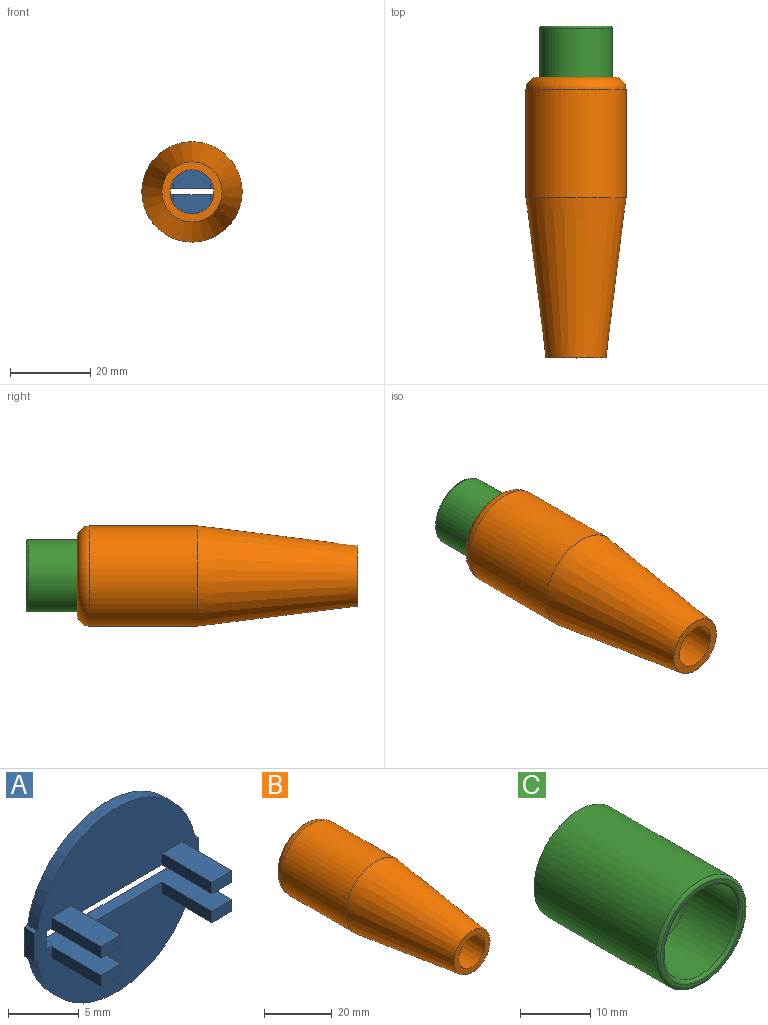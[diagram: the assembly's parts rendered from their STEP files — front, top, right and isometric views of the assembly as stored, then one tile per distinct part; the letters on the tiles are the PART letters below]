
ASSEMBLY  parts=3 mates=2
PART A: 30 faces, bbox 16.5x6x16 mm
  f0: plane 2.5x1mm, normal (1,0,0), area 2.5mm2, adj f1,f11,f12,f13
  f1: plane 1x0.35mm, normal (0,0,1), area 0.3mm2, adj f0,f2,f12,f13
  f2: cylinder r=8mm len=15.8mm, axis (0,1,0), area 22.6mm2, adj f1,f3,f12,f13
  f3: plane 1x0.35mm, normal (0,0,1), area 0.3mm2, adj f2,f4,f12,f13
  f4: plane 2.5x1mm, normal (-1,0,0), area 2.5mm2, adj f3,f5,f12,f13
  f5: plane 1x0.35mm, normal (0,0,-1), area 0.3mm2, adj f4,f6,f12,f13
  f6: cylinder r=8mm len=15.8mm, axis (0,1,0), area 22.6mm2, adj f5,f11,f12,f13
  f7: plane 1.5x1mm, normal (-1,0,0), area 1.5mm2, adj f8,f10,f12,f13
  f8: plane 14x6mm, normal (0,0,1), area 34mm2, adj f7,f9,f12,f13,f18,f19,f21,f22
  f9: plane 1.5x1mm, normal (1,0,0), area 1.5mm2, adj f8,f10,f12,f13
  f10: plane 14x6mm, normal (0,0,-1), area 34mm2, adj f7,f9,f12,f13,f14,f16,f17,f26
  f11: plane 1x0.35mm, normal (0,0,-1), area 0.3mm2, adj f0,f6,f12,f13
  f12: plane 16.5x16mm, normal (0,-1,0), area 173.5mm2, adj f0,f1,f2,f3,f4,f5,f6,f7
  f13: plane 16.5x16mm, normal (0,1,0), area 181.5mm2, adj f0,f1,f2,f3,f4,f5,f6,f7
  f14: plane 5x1mm, normal (1,0,0), area 5mm2, adj f10,f12,f15,f17
  f15: plane 5x2mm, normal (0,0,1), area 10mm2, adj f12,f14,f16,f17
  f16: plane 5x1mm, normal (-1,0,0), area 5mm2, adj f10,f12,f15,f17
  f17: plane 2x1mm, normal (0,-1,0), area 2mm2, adj f10,f14,f15,f16
  f18: plane 5x1mm, normal (1,0,0), area 5mm2, adj f8,f12,f20,f21
  f19: plane 5x1mm, normal (-1,0,0), area 5mm2, adj f8,f12,f20,f21
  f20: plane 5x2mm, normal (0,0,-1), area 10mm2, adj f12,f18,f19,f21
  f21: plane 2x1mm, normal (0,-1,0), area 2mm2, adj f8,f18,f19,f20
  f22: plane 5x1mm, normal (1,0,0), area 5mm2, adj f8,f12,f24,f25
  f23: plane 5x1mm, normal (-1,0,0), area 5mm2, adj f8,f12,f24,f25
  f24: plane 5x2mm, normal (0,0,-1), area 10mm2, adj f12,f22,f23,f25
  f25: plane 2x1mm, normal (0,-1,0), area 2mm2, adj f8,f22,f23,f24
  f26: plane 5x1mm, normal (1,0,0), area 5mm2, adj f10,f12,f27,f29
  f27: plane 5x2mm, normal (0,0,1), area 10mm2, adj f12,f26,f28,f29
  f28: plane 5x1mm, normal (-1,0,0), area 5mm2, adj f10,f12,f27,f29
  f29: plane 2x1mm, normal (0,-1,0), area 2mm2, adj f10,f26,f27,f28
PART B: 8 faces, bbox 27.1x70x27.1 mm
  f0: plane 15x15mm, normal (0,-1,0), area 82.2mm2, adj f1,f2
  f1: cone r=12.5mm half-angle=7.1deg, axis (0,1,0), area 2532.8mm2, adj f0,f5
  f2: cone r=10.52mm half-angle=7.1deg, axis (0,1,0), area 2022.3mm2, adj f0,f3
  f3: plane 20.97x20.97mm, normal (0,-1,0), area 90.9mm2, adj f2,f4
  f4: cylinder r=9mm len=30mm, axis (0,1,0), area 1696.5mm2, adj f3,f6
  f5: cylinder r=12.5mm len=27mm, axis (0,1,0), area 2120.6mm2, adj f1,f7
  f6: plane 19x19mm, normal (0,1,0), area 29.1mm2, adj f4,f7
  f7: torus R=9.5mm, axis (0,-1,0), area 337.8mm2, adj f5,f6
PART C: 15 faces, bbox 19.5x25x19.5 mm
  f0: plane 15x0.35mm, normal (0,0,-1), area 5.2mm2, adj f2,f9,f10,f12
  f1: plane 15x0.35mm, normal (0,0,1), area 5.2mm2, adj f2,f9,f10,f11
  f2: plane 18x18mm, normal (0,1,0), area 52mm2, adj f0,f1,f4,f6,f7,f8,f9,f11
  f3: cylinder r=7.5mm len=15mm, axis (0,1,0), area 447.7mm2, adj f10,f14
  f4: cylinder r=9mm len=24.5mm, axis (0,1,0), area 1385.4mm2, adj f2,f13
  f5: plane 17x17mm, normal (0,-1,0), area 25.9mm2, adj f13,f14
  f6: plane 15x0.35mm, normal (0,0,-1), area 5.2mm2, adj f2,f7,f10,f12
  f7: plane 15x2.5mm, normal (1,0,0), area 37.5mm2, adj f2,f6,f8,f10
  f8: plane 15x0.35mm, normal (0,0,1), area 5.2mm2, adj f2,f7,f10,f11
  f9: plane 15x2.5mm, normal (-1,0,0), area 37.5mm2, adj f0,f1,f2,f10
  f10: plane 16.5x16mm, normal (0,1,0), area 25.8mm2, adj f0,f1,f3,f6,f7,f8,f9,f11
  f11: cylinder r=8mm len=15.8mm, axis (0,1,0), area 339.3mm2, adj f1,f2,f8,f10
  f12: cylinder r=8mm len=15.8mm, axis (0,1,0), area 339.3mm2, adj f0,f2,f6,f10
  f13: torus R=8.5mm, axis (0,-1,0), area 43.5mm2, adj f4,f5
  f14: torus R=8mm, axis (0,-1,0), area 37.9mm2, adj f3,f5
PLACE A t=(9.85,25.38,4.05)mm
PLACE B t=(9.85,22.63,4.05)mm
PLACE C rot(axis=(1,0,0),180deg) t=(9.85,10.38,4.05)mm
MATE fastened A.f2 <-> C.f12  axis (0,1,0) through (9.85,25.38,4.05)mm
MATE slider C.f4 <-> B.f4  axis (0,-1,0) through (9.85,22.63,4.05)mm
